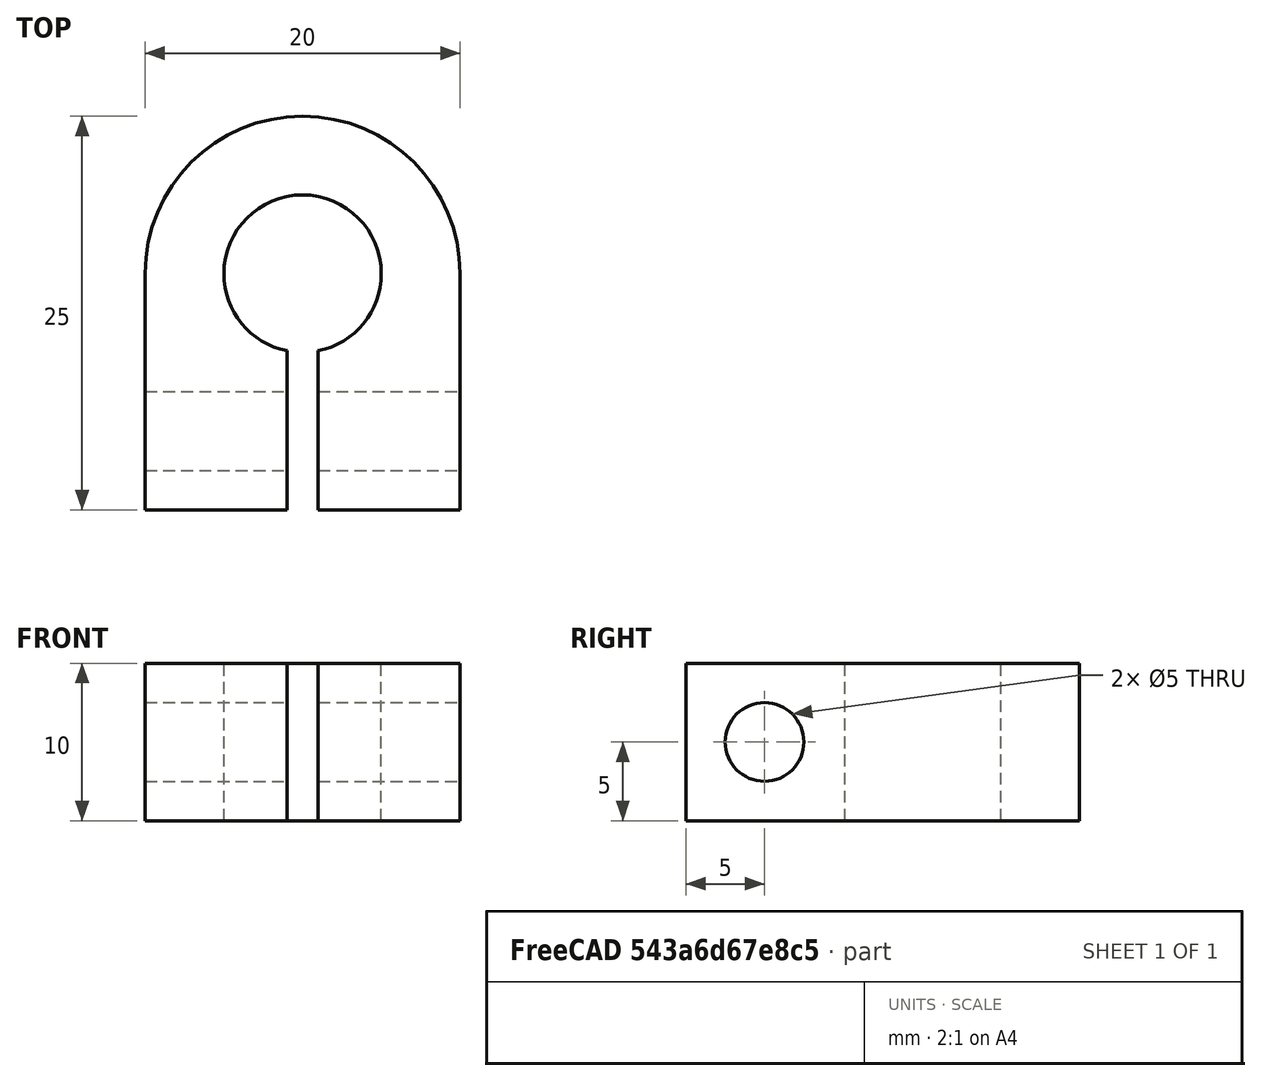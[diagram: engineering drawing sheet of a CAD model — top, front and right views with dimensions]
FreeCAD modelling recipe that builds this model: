
FCSTD DOCUMENT  (FreeCAD 0.18R16110 (Git))
Label: y-end-stop-2x
License: All rights reserved
LicenseURL: http://en.wikipedia.org/wiki/All_rights_reserved
objects: Part::Cylinder×3, Part::Cut×3, Part::Box×2, Part::MultiFuse×1, Mesh::Feature×1
note: 9 computed .brp shape members not serialized (recipe doc carries the construction recipe); baked Part::Feature solids carry a one-line shape summary decoded from their .brp

FEATURE [Part::Cylinder] Cylinder085  label="Zylinder073"
  Angle = 360
  AttacherType = Attacher::AttachEngine3D
  Height = 10
  Radius = 10
FEATURE [Part::Box] Box060  label="Quader039"
  AttacherType = Attacher::AttachEngine3D
  Height = 10
  Length = 2
  Placement = pos=(-1,-15,0) rot=(0,0,1;0rad)
  Width = 15
FEATURE [Part::Box] Box059  label="Quader038"
  AttacherType = Attacher::AttachEngine3D
  Height = 10
  Length = 20
  Placement = pos=(-10,-15,0) rot=(0,0,1;0rad)
  Width = 15
FEATURE [Part::Cylinder] Cylinder088  label="Zylinder076"
  Angle = 360
  AttacherType = Attacher::AttachEngine3D
  Height = 24
  Placement = pos=(-12.5,-10,5) rot=(0,1,0;1.5708rad)
  Radius = 2.5
FEATURE [Part::Cylinder] Cylinder086  label="Zylinder074"
  Angle = 360
  AttacherType = Attacher::AttachEngine3D
  Height = 10
  Radius = 5
FEATURE [Part::MultiFuse] Fusion049
  Shapes = -> [Cylinder085,Box059]
FEATURE [Part::Cut] Cut100
  Base = -> Fusion049
  Tool = -> Box060
FEATURE [Part::Cut] Cut101
  Base = -> Cut100
  Tool = -> Cylinder086
FEATURE [Part::Cut] Cut102  label="y-end-stop-2x"
  Base = -> Cut101
  Tool = -> Cylinder088
FEATURE [Mesh::Feature] Mesh  label="y-end-stop-2x (Meshed)"
